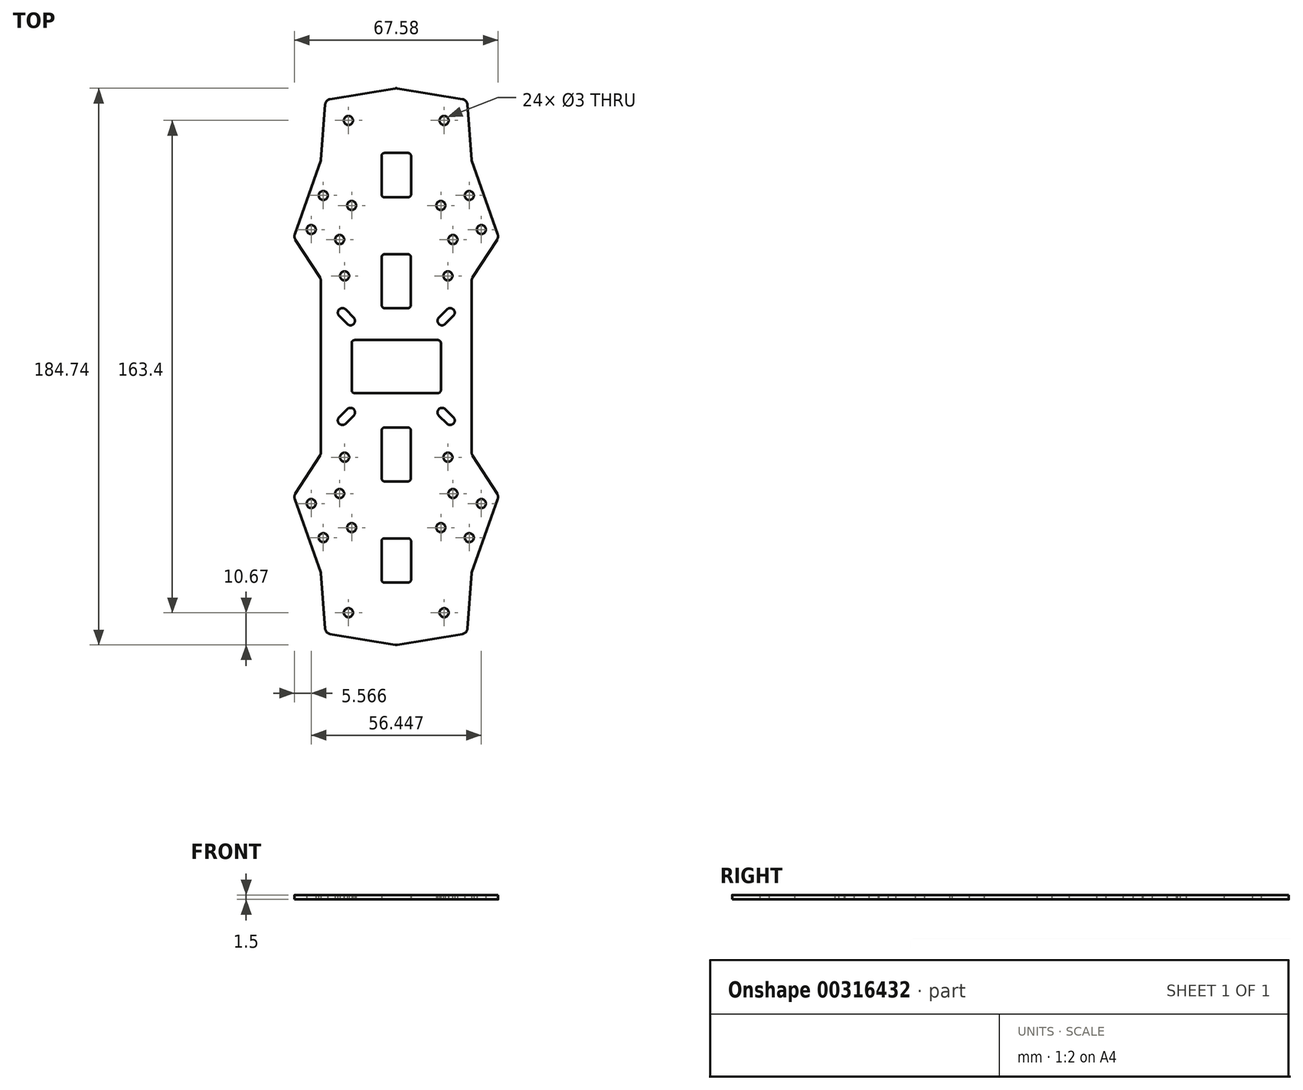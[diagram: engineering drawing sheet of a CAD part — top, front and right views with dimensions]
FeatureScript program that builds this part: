
annotation { "Feature Type Name" : "Feature", "Feature Type Description" : "" }
export const myFeature = defineFeature(function(context is Context, id is Id, definition is map)
    precondition{}
    {
        {
            var Q0;
            Q0=qCreatedBy(makeId("Top.planeOp"),FACE);
            var sketch = newSketch(context, id + "F0", { "sketchPlane" : qUnion([Q0])});
            skLineSegment(sketch, "E0", {"start": v(-25, 28.41) * mm, "end": v(-25, -28.41) * mm});
            skLineSegment(sketch, "E1", {"start": v(-25.32, -29.5) * mm, "end": v(-33.47, -42.18) * mm});
            skLineSegment(sketch, "E2", {"start": v(-33.67, -43.92) * mm, "end": v(-25.04, -68.37) * mm});
            skLineSegment(sketch, "E3", {"start": v(-25, -68.63) * mm, "end": v(-23.62, -86.93) * mm});
            skLineSegment(sketch, "E4", {"start": v(-21.95, -88.76) * mm, "end": v(-0.33, -92.35) * mm});
            skLineSegment(sketch, "E5", {"start": v(0.33, -92.35) * mm, "end": v(21.95, -88.76) * mm});
            skLineSegment(sketch, "E6", {"start": v(23.62, -86.93) * mm, "end": v(25, -68.63) * mm});
            skLineSegment(sketch, "E7", {"start": v(25.04, -68.37) * mm, "end": v(33.67, -43.92) * mm});
            skLineSegment(sketch, "E8", {"start": v(33.47, -42.18) * mm, "end": v(25.32, -29.5) * mm});
            skLineSegment(sketch, "E9", {"start": v(25, -28.41) * mm, "end": v(25, 28.41) * mm});
            skLineSegment(sketch, "E10", {"start": v(25.32, 29.5) * mm, "end": v(33.47, 42.18) * mm});
            skLineSegment(sketch, "E11", {"start": v(33.67, 43.92) * mm, "end": v(25.04, 68.37) * mm});
            skLineSegment(sketch, "E12", {"start": v(25, 68.63) * mm, "end": v(23.62, 86.93) * mm});
            skLineSegment(sketch, "E13", {"start": v(21.95, 88.76) * mm, "end": v(0.33, 92.35) * mm});
            skLineSegment(sketch, "E14", {"start": v(-0.33, 92.35) * mm, "end": v(-21.95, 88.76) * mm});
            skLineSegment(sketch, "E15", {"start": v(-23.62, 86.93) * mm, "end": v(-25, 68.63) * mm});
            skLineSegment(sketch, "E16", {"start": v(-25.04, 68.37) * mm, "end": v(-33.67, 43.92) * mm});
            skLineSegment(sketch, "E17", {"start": v(-33.47, 42.18) * mm, "end": v(-25.32, 29.5) * mm});
            skLineSegment(sketch, "E18.bottom", {"start": v(-13.8, 8.8) * mm, "end": v(13.8, 8.8) * mm});
            skLineSegment(sketch, "E18.top", {"start": v(-13.8, -8.8) * mm, "end": v(13.8, -8.8) * mm});
            skLineSegment(sketch, "E18.left", {"start": v(-14.8, 7.8) * mm, "end": v(-14.8, -7.8) * mm});
            skLineSegment(sketch, "E18.right", {"start": v(14.8, 7.8) * mm, "end": v(14.8, -7.8) * mm});
            skPoint(sketch, "E18.middle", {"position": v(0, 0) * mm});
            skPoint(sketch, "E19.visualSharp", {"position": v(-14.8, 8.8) * mm});
            skArc(sketch, "E19.filletArc", {"start": v(-13.8, 8.8) * mm, "mid": v(-14.5, 8.5) * mm, "end": v(-14.8, 7.8) * mm});
            skPoint(sketch, "E20.visualSharp", {"position": v(14.8, 8.8) * mm});
            skArc(sketch, "E20.filletArc", {"start": v(14.8, 7.8) * mm, "mid": v(14.5, 8.5) * mm, "end": v(13.8, 8.8) * mm});
            skPoint(sketch, "E21.visualSharp", {"position": v(14.8, -8.8) * mm});
            skArc(sketch, "E21.filletArc", {"start": v(13.8, -8.8) * mm, "mid": v(14.5, -8.5) * mm, "end": v(14.8, -7.8) * mm});
            skPoint(sketch, "E22.visualSharp", {"position": v(-14.8, -8.8) * mm});
            skArc(sketch, "E22.filletArc", {"start": v(-14.8, -7.8) * mm, "mid": v(-14.5, -8.5) * mm, "end": v(-13.8, -8.8) * mm});
            skLineSegment(sketch, "E23.bottom", {"start": v(-3.85, 19.4) * mm, "end": v(3.85, 19.4) * mm});
            skLineSegment(sketch, "E23.top", {"start": v(-3.85, 37.3) * mm, "end": v(3.85, 37.3) * mm});
            skLineSegment(sketch, "E23.left", {"start": v(-4.85, 20.4) * mm, "end": v(-4.85, 36.3) * mm});
            skLineSegment(sketch, "E23.right", {"start": v(4.85, 20.4) * mm, "end": v(4.85, 36.3) * mm});
            skPoint(sketch, "E23.middle", {"position": v(0, 28.35) * mm});
            skPoint(sketch, "E24.visualSharp", {"position": v(-4.85, 37.3) * mm});
            skArc(sketch, "E24.filletArc", {"start": v(-3.85, 37.3) * mm, "mid": v(-4.56, 37) * mm, "end": v(-4.85, 36.3) * mm});
            skPoint(sketch, "E25.visualSharp", {"position": v(4.85, 37.3) * mm});
            skArc(sketch, "E25.filletArc", {"start": v(4.85, 36.3) * mm, "mid": v(4.56, 37) * mm, "end": v(3.85, 37.3) * mm});
            skPoint(sketch, "E26.visualSharp", {"position": v(4.85, 19.4) * mm});
            skArc(sketch, "E26.filletArc", {"start": v(3.85, 19.4) * mm, "mid": v(4.56, 19.7) * mm, "end": v(4.85, 20.4) * mm});
            skPoint(sketch, "E27.visualSharp", {"position": v(-4.85, 19.4) * mm});
            skArc(sketch, "E27.filletArc", {"start": v(-4.85, 20.4) * mm, "mid": v(-4.56, 19.7) * mm, "end": v(-3.85, 19.4) * mm});
            skLineSegment(sketch, "E28.bottom", {"start": v(-3.9, 56.2) * mm, "end": v(3.9, 56.2) * mm});
            skLineSegment(sketch, "E28.top", {"start": v(-3.9, 70.9) * mm, "end": v(3.9, 70.9) * mm});
            skLineSegment(sketch, "E28.left", {"start": v(-4.9, 57.2) * mm, "end": v(-4.9, 69.9) * mm});
            skLineSegment(sketch, "E28.right", {"start": v(4.9, 57.2) * mm, "end": v(4.9, 69.9) * mm});
            skPoint(sketch, "E28.middle", {"position": v(0, 63.55) * mm});
            skPoint(sketch, "E29.visualSharp", {"position": v(4.9, 56.2) * mm});
            skArc(sketch, "E29.filletArc", {"start": v(3.9, 56.2) * mm, "mid": v(4.6, 56.5) * mm, "end": v(4.9, 57.2) * mm});
            skPoint(sketch, "E30.visualSharp", {"position": v(-4.9, 56.2) * mm});
            skArc(sketch, "E30.filletArc", {"start": v(-4.9, 57.2) * mm, "mid": v(-4.6, 56.5) * mm, "end": v(-3.9, 56.2) * mm});
            skPoint(sketch, "E31.visualSharp", {"position": v(-4.9, 70.9) * mm});
            skArc(sketch, "E31.filletArc", {"start": v(-3.9, 70.9) * mm, "mid": v(-4.6, 70.6) * mm, "end": v(-4.9, 69.9) * mm});
            skPoint(sketch, "E32.visualSharp", {"position": v(4.9, 70.9) * mm});
            skArc(sketch, "E32.filletArc", {"start": v(4.9, 69.9) * mm, "mid": v(4.6, 70.6) * mm, "end": v(3.9, 70.9) * mm});
            skPoint(sketch, "E33.visualSharp", {"position": v(-34, -43) * mm});
            skArc(sketch, "E33.filletArc", {"start": v(-33.47, -42.18) * mm, "mid": v(-33.77, -43.03) * mm, "end": v(-33.67, -43.92) * mm});
            skPoint(sketch, "E34.visualSharp", {"position": v(34, -43) * mm});
            skArc(sketch, "E34.filletArc", {"start": v(33.67, -43.92) * mm, "mid": v(33.77, -43.03) * mm, "end": v(33.47, -42.18) * mm});
            skPoint(sketch, "E35.visualSharp", {"position": v(25, -29) * mm});
            skArc(sketch, "E35.filletArc", {"start": v(25, -28.41) * mm, "mid": v(25.08, -28.98) * mm, "end": v(25.32, -29.5) * mm});
            skPoint(sketch, "E36.visualSharp", {"position": v(-25, -29) * mm});
            skArc(sketch, "E36.filletArc", {"start": v(-25.32, -29.5) * mm, "mid": v(-25.08, -28.98) * mm, "end": v(-25, -28.41) * mm});
            skPoint(sketch, "E37.visualSharp", {"position": v(-25, -68.5) * mm});
            skArc(sketch, "E37.filletArc", {"start": v(-25, -68.63) * mm, "mid": v(-25, -68.5) * mm, "end": v(-25.04, -68.37) * mm});
            skPoint(sketch, "E38.visualSharp", {"position": v(25, -68.5) * mm});
            skArc(sketch, "E38.filletArc", {"start": v(25.04, -68.37) * mm, "mid": v(25, -68.5) * mm, "end": v(25, -68.63) * mm});
            skPoint(sketch, "E39.visualSharp", {"position": v(23.5, -88.5) * mm});
            skArc(sketch, "E39.filletArc", {"start": v(21.95, -88.76) * mm, "mid": v(23.1, -88.13) * mm, "end": v(23.62, -86.93) * mm});
            skPoint(sketch, "E40.visualSharp", {"position": v(-23.5, -88.5) * mm});
            skArc(sketch, "E40.filletArc", {"start": v(-23.62, -86.93) * mm, "mid": v(-23.1, -88.13) * mm, "end": v(-21.95, -88.76) * mm});
            skPoint(sketch, "E41.visualSharp", {"position": v(0, -92.4) * mm});
            skArc(sketch, "E41.filletArc", {"start": v(-0.33, -92.35) * mm, "mid": v(0, -92.37) * mm, "end": v(0.33, -92.35) * mm});
            skPoint(sketch, "E42.visualSharp", {"position": v(25, 29) * mm});
            skArc(sketch, "E42.filletArc", {"start": v(25.32, 29.5) * mm, "mid": v(25.08, 28.98) * mm, "end": v(25, 28.41) * mm});
            skPoint(sketch, "E43.visualSharp", {"position": v(-25, 29) * mm});
            skArc(sketch, "E43.filletArc", {"start": v(-25, 28.41) * mm, "mid": v(-25.08, 28.98) * mm, "end": v(-25.32, 29.5) * mm});
            skPoint(sketch, "E44.visualSharp", {"position": v(34, 43) * mm});
            skArc(sketch, "E44.filletArc", {"start": v(33.47, 42.18) * mm, "mid": v(33.77, 43.03) * mm, "end": v(33.67, 43.92) * mm});
            skPoint(sketch, "E45.visualSharp", {"position": v(-34, 43) * mm});
            skArc(sketch, "E45.filletArc", {"start": v(-33.67, 43.92) * mm, "mid": v(-33.77, 43.03) * mm, "end": v(-33.47, 42.18) * mm});
            skPoint(sketch, "E46.visualSharp", {"position": v(-25, 68.5) * mm});
            skArc(sketch, "E46.filletArc", {"start": v(-25.04, 68.37) * mm, "mid": v(-25, 68.5) * mm, "end": v(-25, 68.63) * mm});
            skPoint(sketch, "E47.visualSharp", {"position": v(25, 68.5) * mm});
            skArc(sketch, "E47.filletArc", {"start": v(25, 68.63) * mm, "mid": v(25, 68.5) * mm, "end": v(25.04, 68.37) * mm});
            skPoint(sketch, "E48.visualSharp", {"position": v(23.5, 88.5) * mm});
            skArc(sketch, "E48.filletArc", {"start": v(23.62, 86.93) * mm, "mid": v(23.1, 88.13) * mm, "end": v(21.95, 88.76) * mm});
            skPoint(sketch, "E49.visualSharp", {"position": v(-23.5, 88.5) * mm});
            skArc(sketch, "E49.filletArc", {"start": v(-21.95, 88.76) * mm, "mid": v(-23.1, 88.13) * mm, "end": v(-23.62, 86.93) * mm});
            skPoint(sketch, "E50.visualSharp", {"position": v(0, 92.4) * mm});
            skArc(sketch, "E50.filletArc", {"start": v(0.33, 92.35) * mm, "mid": v(0, 92.37) * mm, "end": v(-0.33, 92.35) * mm});
            skArc(sketch, "E51.MirrorCS", {"start": v(4.85, 20.4) * mm, "mid": v(4.56, 19.7) * mm, "end": v(3.85, 19.4) * mm});
            skArc(sketch, "E52.MirrorCS", {"start": v(-3.85, 19.4) * mm, "mid": v(-4.56, 19.7) * mm, "end": v(-4.85, 20.4) * mm});
            skLineSegment(sketch, "E53.MirrorCS", {"start": v(3.85, 19.4) * mm, "end": v(-3.85, 19.4) * mm});
            skCircle(sketch, "E54", {"center": v(-17.15, 30.1) * mm, "radius": 1.5 * mm});
            skCircle(sketch, "E55.MirrorC", {"center": v(-17.15, -30.1) * mm, "radius": 1.5 * mm});
            skCircle(sketch, "E56.MirrorC", {"center": v(17.15, -30.1) * mm, "radius": 1.5 * mm});
            skCircle(sketch, "E57.MirrorC", {"center": v(17.15, 30.1) * mm, "radius": 1.5 * mm});
            skCircle(sketch, "E58", {"center": v(-15.88, 81.7) * mm, "radius": 1.5 * mm});
            skCircle(sketch, "E59.MirrorC", {"center": v(15.88, 81.7) * mm, "radius": 1.5 * mm});
            skCircle(sketch, "E60.MirrorC", {"center": v(15.88, -81.7) * mm, "radius": 1.5 * mm});
            skCircle(sketch, "E61.MirrorC", {"center": v(-15.88, -81.7) * mm, "radius": 1.5 * mm});
            skLineSegment(sketch, "E62", {"start": v(-17.89, 17.89) * mm, "end": v(-15.2, 15.2) * mm});
            skArc(sketch, "E63.0.startCap", {"start": v(-18.95, 16.83) * mm, "mid": v(-18.95, 18.95) * mm, "end": v(-16.83, 18.95) * mm});
            skArc(sketch, "E63.0.endCap", {"start": v(-14.14, 16.26) * mm, "mid": v(-14.14, 14.14) * mm, "end": v(-16.26, 14.14) * mm});
            skLineSegment(sketch, "E63.0.left", {"start": v(-16.83, 18.95) * mm, "end": v(-14.14, 16.26) * mm});
            skLineSegment(sketch, "E63.0.right", {"start": v(-18.95, 16.83) * mm, "end": v(-16.26, 14.14) * mm});
            skLineSegment(sketch, "E64.MirrorCS", {"start": v(18.95, 16.83) * mm, "end": v(16.26, 14.14) * mm});
            skLineSegment(sketch, "E65.MirrorCS", {"start": v(17.89, 17.89) * mm, "end": v(15.2, 15.2) * mm});
            skLineSegment(sketch, "E66.MirrorCS", {"start": v(16.83, 18.95) * mm, "end": v(14.14, 16.26) * mm});
            skArc(sketch, "E67.MirrorCS", {"start": v(18.95, 16.83) * mm, "mid": v(18.95, 18.95) * mm, "end": v(16.83, 18.95) * mm});
            skArc(sketch, "E68.MirrorCS", {"start": v(14.14, 16.26) * mm, "mid": v(14.14, 14.14) * mm, "end": v(16.26, 14.14) * mm});
            skLineSegment(sketch, "E69.MirrorCS", {"start": v(-16.83, -18.95) * mm, "end": v(-14.14, -16.26) * mm});
            skLineSegment(sketch, "E70.MirrorCS", {"start": v(-17.89, -17.89) * mm, "end": v(-15.2, -15.2) * mm});
            skArc(sketch, "E71.MirrorCS", {"start": v(-14.14, -16.26) * mm, "mid": v(-14.14, -14.14) * mm, "end": v(-16.26, -14.14) * mm});
            skLineSegment(sketch, "E72.MirrorCS", {"start": v(-18.95, -16.83) * mm, "end": v(-16.26, -14.14) * mm});
            skArc(sketch, "E73.MirrorCS", {"start": v(-18.95, -16.83) * mm, "mid": v(-18.95, -18.95) * mm, "end": v(-16.83, -18.95) * mm});
            skLineSegment(sketch, "E74.MirrorCS", {"start": v(17.89, -17.89) * mm, "end": v(15.2, -15.2) * mm});
            skLineSegment(sketch, "E75.MirrorCS", {"start": v(18.95, -16.83) * mm, "end": v(16.26, -14.14) * mm});
            skLineSegment(sketch, "E76.MirrorCS", {"start": v(16.83, -18.95) * mm, "end": v(14.14, -16.26) * mm});
            skArc(sketch, "E77.MirrorCS", {"start": v(18.95, -16.83) * mm, "mid": v(18.95, -18.95) * mm, "end": v(16.83, -18.95) * mm});
            skArc(sketch, "E78.MirrorCS", {"start": v(14.14, -16.26) * mm, "mid": v(14.14, -14.14) * mm, "end": v(16.26, -14.14) * mm});
            skLineSegment(sketch, "E79", {"start": v(-24.34, 50.47) * mm, "end": v(-21.51, 49.47) * mm});
            skLineSegment(sketch, "E80", {"start": v(-21.51, 49.47) * mm, "end": v(-20.51, 52.3) * mm});
            skCircle(sketch, "E81", {"center": v(-18.8, 42.15) * mm, "radius": 1.5 * mm});
            skCircle(sketch, "E82.MirrorC", {"center": v(-14.8, 53.47) * mm, "radius": 1.5 * mm});
            skCircle(sketch, "E83.MirrorC", {"center": v(-24.23, 56.8) * mm, "radius": 1.5 * mm});
            skCircle(sketch, "E84.MirrorC", {"center": v(-28.22, 45.48) * mm, "radius": 1.5 * mm});
            skCircle(sketch, "E85.MirrorC", {"center": v(14.8, 53.47) * mm, "radius": 1.5 * mm});
            skCircle(sketch, "E86.MirrorC", {"center": v(24.23, 56.8) * mm, "radius": 1.5 * mm});
            skCircle(sketch, "E87.MirrorC", {"center": v(28.22, 45.48) * mm, "radius": 1.5 * mm});
            skLineSegment(sketch, "E88.MirrorCS", {"start": v(24.34, 50.47) * mm, "end": v(21.51, 49.47) * mm});
            skLineSegment(sketch, "E89.MirrorCS", {"start": v(21.51, 49.47) * mm, "end": v(20.51, 52.3) * mm});
            skCircle(sketch, "E90.MirrorC", {"center": v(18.8, 42.15) * mm, "radius": 1.5 * mm});
            skLineSegment(sketch, "E91.MirrorCS", {"start": v(21.51, -49.47) * mm, "end": v(20.51, -52.3) * mm});
            skLineSegment(sketch, "E92.MirrorCS", {"start": v(24.34, -50.47) * mm, "end": v(21.51, -49.47) * mm});
            skCircle(sketch, "E93.MirrorC", {"center": v(24.23, -56.8) * mm, "radius": 1.5 * mm});
            skCircle(sketch, "E94.MirrorC", {"center": v(28.22, -45.48) * mm, "radius": 1.5 * mm});
            skCircle(sketch, "E95.MirrorC", {"center": v(18.8, -42.15) * mm, "radius": 1.5 * mm});
            skCircle(sketch, "E96.MirrorC", {"center": v(14.8, -53.47) * mm, "radius": 1.5 * mm});
            skCircle(sketch, "E97.MirrorC", {"center": v(-18.8, -42.15) * mm, "radius": 1.5 * mm});
            skCircle(sketch, "E98.MirrorC", {"center": v(-28.22, -45.48) * mm, "radius": 1.5 * mm});
            skLineSegment(sketch, "E99.MirrorCS", {"start": v(-21.51, -49.47) * mm, "end": v(-20.51, -52.3) * mm});
            skLineSegment(sketch, "E100.MirrorCS", {"start": v(-24.34, -50.47) * mm, "end": v(-21.51, -49.47) * mm});
            skCircle(sketch, "E101.MirrorC", {"center": v(-24.23, -56.8) * mm, "radius": 1.5 * mm});
            skCircle(sketch, "E102.MirrorC", {"center": v(-14.8, -53.47) * mm, "radius": 1.5 * mm});
            skLineSegment(sketch, "E103", {"start": v(-5, -0.4) * mm, "end": v(5, -0.4) * mm});
            skArc(sketch, "E104.MirrorCS", {"start": v(4.85, -21.2) * mm, "mid": v(4.56, -20.5) * mm, "end": v(3.85, -20.2) * mm});
            skArc(sketch, "E105.MirrorCS", {"start": v(-3.85, -20.2) * mm, "mid": v(-4.56, -20.5) * mm, "end": v(-4.85, -21.2) * mm});
            skArc(sketch, "E106.MirrorCS", {"start": v(3.85, -20.2) * mm, "mid": v(4.56, -20.5) * mm, "end": v(4.85, -21.2) * mm});
            skArc(sketch, "E107.MirrorCS", {"start": v(-4.85, -21.2) * mm, "mid": v(-4.56, -20.5) * mm, "end": v(-3.85, -20.2) * mm});
            skArc(sketch, "E108.MirrorCS", {"start": v(4.85, -37.1) * mm, "mid": v(4.56, -37.8) * mm, "end": v(3.85, -38.1) * mm});
            skArc(sketch, "E109.MirrorCS", {"start": v(-3.85, -38.1) * mm, "mid": v(-4.56, -37.8) * mm, "end": v(-4.85, -37.1) * mm});
            skLineSegment(sketch, "E110.MirrorCS", {"start": v(-3.85, -20.2) * mm, "end": v(3.85, -20.2) * mm});
            skPoint(sketch, "E111.MirrorP", {"position": v(-4.85, -20.2) * mm});
            skPoint(sketch, "E112.MirrorP", {"position": v(4.85, -20.2) * mm});
            skPoint(sketch, "E113.MirrorP", {"position": v(0, -29.15) * mm});
            skLineSegment(sketch, "E114.MirrorCS", {"start": v(3.85, -20.2) * mm, "end": v(-3.85, -20.2) * mm});
            skLineSegment(sketch, "E115.MirrorCS", {"start": v(-4.85, -21.2) * mm, "end": v(-4.85, -37.1) * mm});
            skLineSegment(sketch, "E116.MirrorCS", {"start": v(-3.85, -38.1) * mm, "end": v(3.85, -38.1) * mm});
            skLineSegment(sketch, "E117.MirrorCS", {"start": v(4.85, -21.2) * mm, "end": v(4.85, -37.1) * mm});
            skPoint(sketch, "E118.MirrorP", {"position": v(-4.85, -38.1) * mm});
            skPoint(sketch, "E119.MirrorP", {"position": v(4.85, -38.1) * mm});
            skArc(sketch, "E120.MirrorCS", {"start": v(3.9, -57) * mm, "mid": v(4.6, -57.3) * mm, "end": v(4.9, -58) * mm});
            skArc(sketch, "E121.MirrorCS", {"start": v(-4.9, -58) * mm, "mid": v(-4.6, -57.3) * mm, "end": v(-3.9, -57) * mm});
            skArc(sketch, "E122.MirrorCS", {"start": v(-3.9, -71.7) * mm, "mid": v(-4.6, -71.4) * mm, "end": v(-4.9, -70.7) * mm});
            skArc(sketch, "E123.MirrorCS", {"start": v(4.9, -70.7) * mm, "mid": v(4.6, -71.4) * mm, "end": v(3.9, -71.7) * mm});
            skLineSegment(sketch, "E124.MirrorCS", {"start": v(-4.9, -58) * mm, "end": v(-4.9, -70.7) * mm});
            skPoint(sketch, "E125.MirrorP", {"position": v(4.9, -71.7) * mm});
            skLineSegment(sketch, "E126.MirrorCS", {"start": v(-3.9, -57) * mm, "end": v(3.9, -57) * mm});
            skPoint(sketch, "E127.MirrorP", {"position": v(-4.9, -71.7) * mm});
            skPoint(sketch, "E128.MirrorP", {"position": v(-4.9, -57) * mm});
            skLineSegment(sketch, "E129.MirrorCS", {"start": v(-3.9, -71.7) * mm, "end": v(3.9, -71.7) * mm});
            skLineSegment(sketch, "E130.MirrorCS", {"start": v(4.9, -58) * mm, "end": v(4.9, -70.7) * mm});
            skPoint(sketch, "E131.MirrorP", {"position": v(0, -64.35) * mm});
            skPoint(sketch, "E132.MirrorP", {"position": v(4.9, -57) * mm});
            skSolve(sketch);
        }
        {
            var Q0;
            Q0 = qSketchRegion(id + "F0", true);
            extrude(context, id + "F1", {"entities" : qUnion([Q0]), "depth" : 1.5 * mm});
        }
    });
